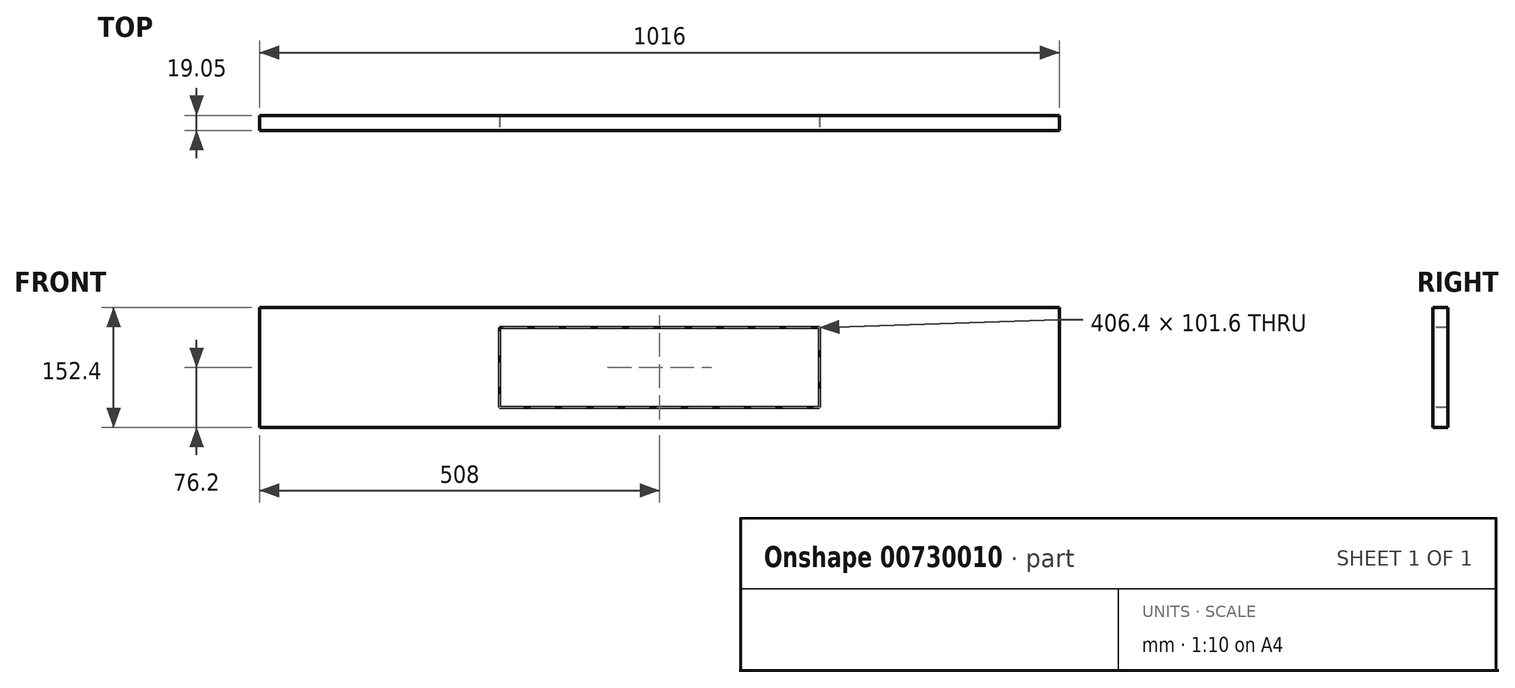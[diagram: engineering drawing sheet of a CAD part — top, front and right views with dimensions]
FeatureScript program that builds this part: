
annotation { "Feature Type Name" : "Feature", "Feature Type Description" : "" }
export const myFeature = defineFeature(function(context is Context, id is Id, definition is map)
    precondition{}
    {
        {
            var Q0;
            Q0=qCreatedBy(makeId("Front.planeOp"),FACE);
            var sketch = newSketch(context, id + "F0", { "sketchPlane" : qUnion([Q0])});
            skLineSegment(sketch, "E0.bottom", {"start": v(203.2, 50.8) * mm, "end": v(-203.2, 50.8) * mm});
            skLineSegment(sketch, "E0.top", {"start": v(203.2, -50.8) * mm, "end": v(-203.2, -50.8) * mm});
            skLineSegment(sketch, "E0.left", {"start": v(203.2, 50.8) * mm, "end": v(203.2, -50.8) * mm});
            skLineSegment(sketch, "E0.right", {"start": v(-203.2, 50.8) * mm, "end": v(-203.2, -50.8) * mm});
            skPoint(sketch, "E0.middle", {"position": v(0, 0) * mm});
            skSolve(sketch);
        }
        {
            var Q0;
            Q0=qCreatedBy(makeId("Front.planeOp"),FACE);
            var sketch = newSketch(context, id + "F1", { "sketchPlane" : qUnion([Q0])});
            skLineSegment(sketch, "E1.bottom", {"start": v(508, 76.2) * mm, "end": v(-508, 76.2) * mm});
            skLineSegment(sketch, "E1.top", {"start": v(508, -76.2) * mm, "end": v(-508, -76.2) * mm});
            skLineSegment(sketch, "E1.left", {"start": v(508, 76.2) * mm, "end": v(508, -76.2) * mm});
            skLineSegment(sketch, "E1.right", {"start": v(-508, 76.2) * mm, "end": v(-508, -76.2) * mm});
            skPoint(sketch, "E1.middle", {"position": v(0, 0) * mm});
            skSolve(sketch);
        }
        {
            var Q0;
            Q0=makeQuery(id+"F1.imprint","IMPRINT",FACE,{"disambiguationData":[TD([[makeQuery(id+"F1.imprint","IMPRINT",EDGE,{"derivedFrom":sQuery(id+"F1.wireOp",EDGE,"E1.bottom")}),1.0]])]});
            extrude(context, id + "F2", {"entities" : qUnion([Q0]), "oppositeDirection" : true, "depth" : 19.05 * mm, "offsetDistance" : 25.4 * mm});
        }
        {
            var Q0;
            Q0=makeQuery(id+"F0.imprint","IMPRINT",FACE,{"disambiguationData":[TD([[makeQuery(id+"F0.imprint","IMPRINT",EDGE,{"derivedFrom":sQuery(id+"F0.wireOp",EDGE,"E0.bottom")}),1.0]])]});
            extrude(context, id + "F3", {"entities" : qUnion([Q0]), "operationType" : NewBodyOperationType.REMOVE, "oppositeDirection" : true, "depth" : 19.05 * mm, "offsetDistance" : 25.4 * mm});
        }
    });
